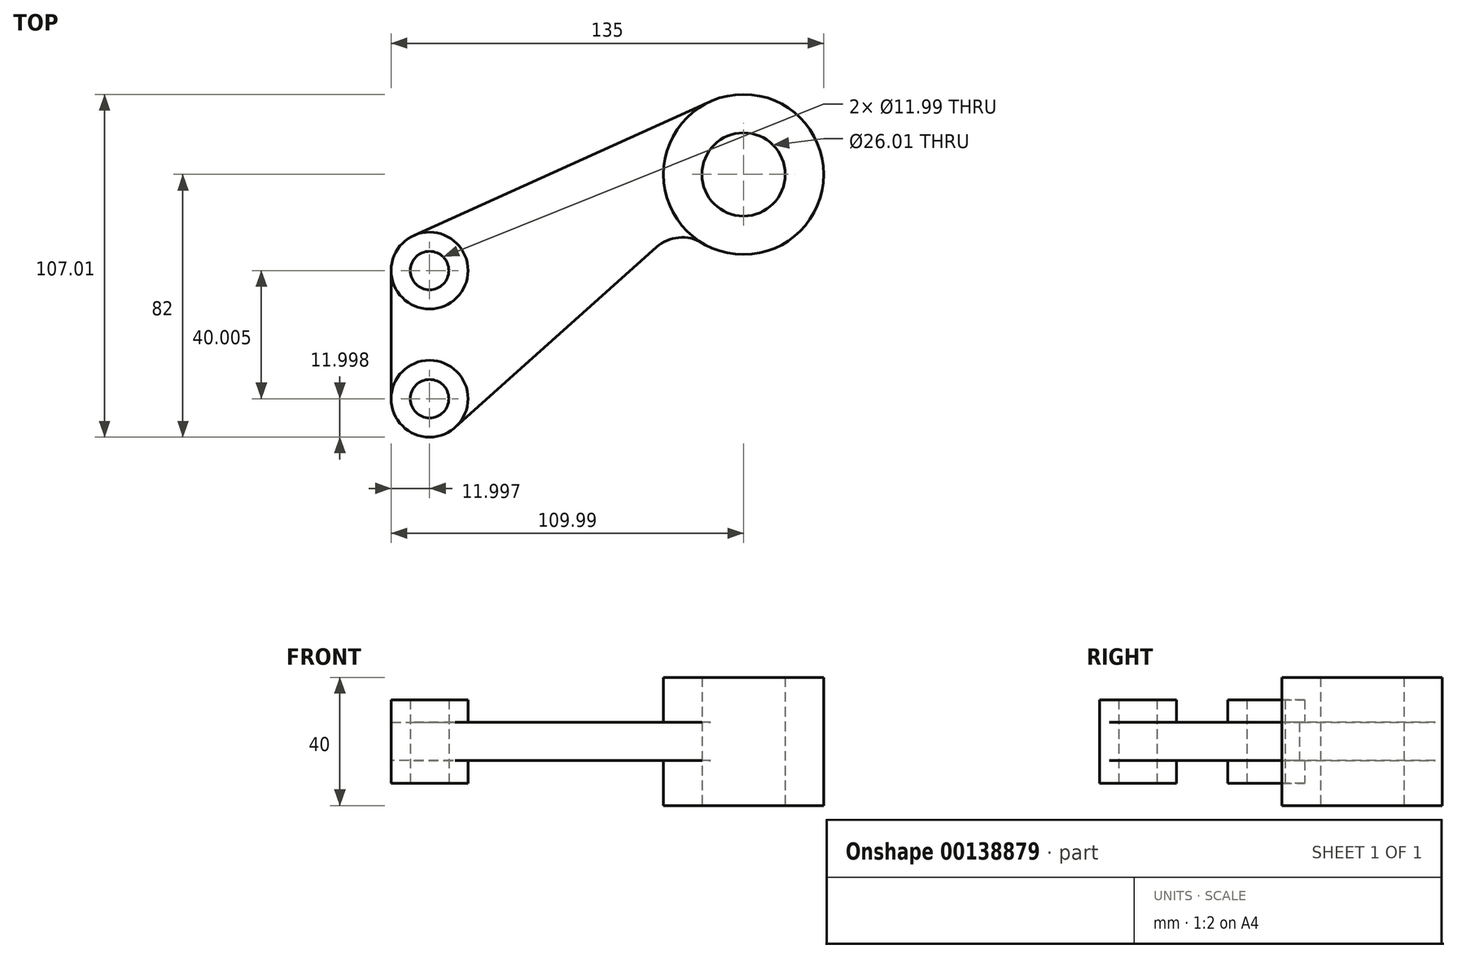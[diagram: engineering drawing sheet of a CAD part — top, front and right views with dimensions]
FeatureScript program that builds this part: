
annotation { "Feature Type Name" : "Feature", "Feature Type Description" : "" }
export const myFeature = defineFeature(function(context is Context, id is Id, definition is map)
    precondition{}
    {
        {
            var Q0;
            Q0=qCreatedBy(makeId("Top.planeOp"),FACE);
            var sketch = newSketch(context, id + "F0", { "sketchPlane" : qUnion([Q0])});
            skCircle(sketch, "E0", {"center": v(0, 0) * mm, "radius": 13 * mm});
            skCircle(sketch, "E1", {"center": v(0, 0) * mm, "radius": 25 * mm});
            skCircle(sketch, "E2", {"center": v(-98, -70) * mm, "radius": 6 * mm});
            skCircle(sketch, "E3", {"center": v(-98, -70) * mm, "radius": 12 * mm});
            skCircle(sketch, "E4", {"center": v(-98, -30) * mm, "radius": 6 * mm});
            skCircle(sketch, "E5", {"center": v(-98, -30) * mm, "radius": 12 * mm});
            skLineSegment(sketch, "E6", {"start": v(-102.93, -19.06) * mm, "end": v(-10.3, 22.79) * mm});
            skArc(sketch, "E7", {"start": v(-12.95, -21.4) * mm, "mid": v(-20.27, -19.71) * mm, "end": v(-27.15, -22.71) * mm});
            skLineSegment(sketch, "E8", {"start": v(-27.15, -22.71) * mm, "end": v(-90, -78.95) * mm});
            skLineSegment(sketch, "E9", {"start": v(-110, -30) * mm, "end": v(-110, -70) * mm});
            skSolve(sketch);
        }
        {
            var Q0;
            Q0=makeQuery(id+"F0.imprint","IMPRINT",FACE,{"disambiguationData":[TD([[makeQuery(id+"F0.imprint","IMPRINT",EDGE,{"derivedFrom":sQuery(id+"F0.wireOp",EDGE,"E0")}),-1.0]])]});
            extrude(context, id + "F1", {"entities" : qUnion([Q0]), "endBound" : BoundingType.SYMMETRIC, "depth" : 40 * mm});
        }
        {
            var Q0;
            {var subQ0=sQuery(id+"F0.wireOp",EDGE,"E6");Q0=makeQuery(id+"F0.imprint","IMPRINT",FACE,{"disambiguationData":[TD([[makeQuery(id+"F0.imprint","IMPRINT",EDGE,{"derivedFrom":subQ0}),-1.0]])]});}
            extrude(context, id + "F2", {"entities" : qUnion([Q0]), "operationType" : NewBodyOperationType.ADD, "endBound" : BoundingType.SYMMETRIC, "depth" : 12 * mm});
        }
        {
            var Q0;
            Q0=makeQuery(id+"F0.imprint","IMPRINT",FACE,{"disambiguationData":[TD([[makeQuery(id+"F0.imprint","IMPRINT",EDGE,{"derivedFrom":sQuery(id+"F0.wireOp",EDGE,"E4")}),-1.0]])]});
            var Q1;
            Q1=makeQuery(id+"F0.imprint","IMPRINT",FACE,{"disambiguationData":[TD([[makeQuery(id+"F0.imprint","IMPRINT",EDGE,{"derivedFrom":sQuery(id+"F0.wireOp",EDGE,"E2")}),-1.0]])]});
            extrude(context, id + "F3", {"entities" : qUnion([Q0, Q1]), "operationType" : NewBodyOperationType.ADD, "endBound" : BoundingType.SYMMETRIC, "depth" : 26 * mm});
        }
    });
